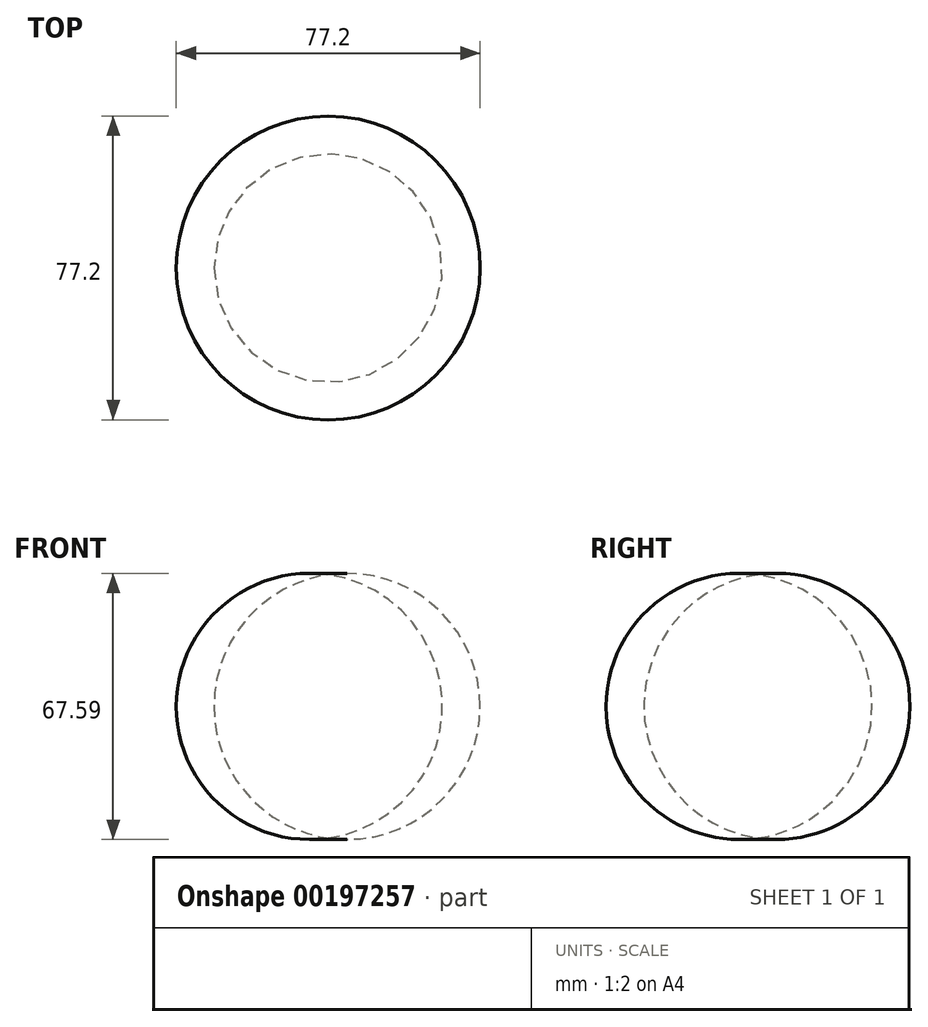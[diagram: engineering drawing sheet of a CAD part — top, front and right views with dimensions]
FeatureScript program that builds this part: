
annotation { "Feature Type Name" : "Feature", "Feature Type Description" : "" }
export const myFeature = defineFeature(function(context is Context, id is Id, definition is map)
    precondition{}
    {
        {
            var Q0;
            Q0=qCreatedBy(makeId("Front.planeOp"),FACE);
            var sketch = newSketch(context, id + "F0", { "sketchPlane" : qUnion([Q0])});
            skLineSegment(sketch, "E0", {"start": v(0, 56.18) * mm, "end": v(0, -10.72) * mm});
            skArc(sketch, "E1", {"start": v(0, 56.18) * mm, "mid": v(-38.6, 22.73) * mm, "end": v(0, -10.72) * mm});
            skSolve(sketch);
        }
        {
            var Q0;
            Q0=makeQuery(id+"F0.imprint","IMPRINT",FACE,{"disambiguationData":[TD([[makeQuery(id+"F0.imprint","IMPRINT",EDGE,{"derivedFrom":sQuery(id+"F0.wireOp",EDGE,"E0")}),-1.0]])]});
            var Q1;
            Q1=sQuery(id+"F0.wireOp",EDGE,"E0");
            revolve(context, id + "F1", {"entities" : qUnion([Q0]), "axis" : qUnion([Q1]), "revolveType" : RevolveType.FULL});
        }
    });
